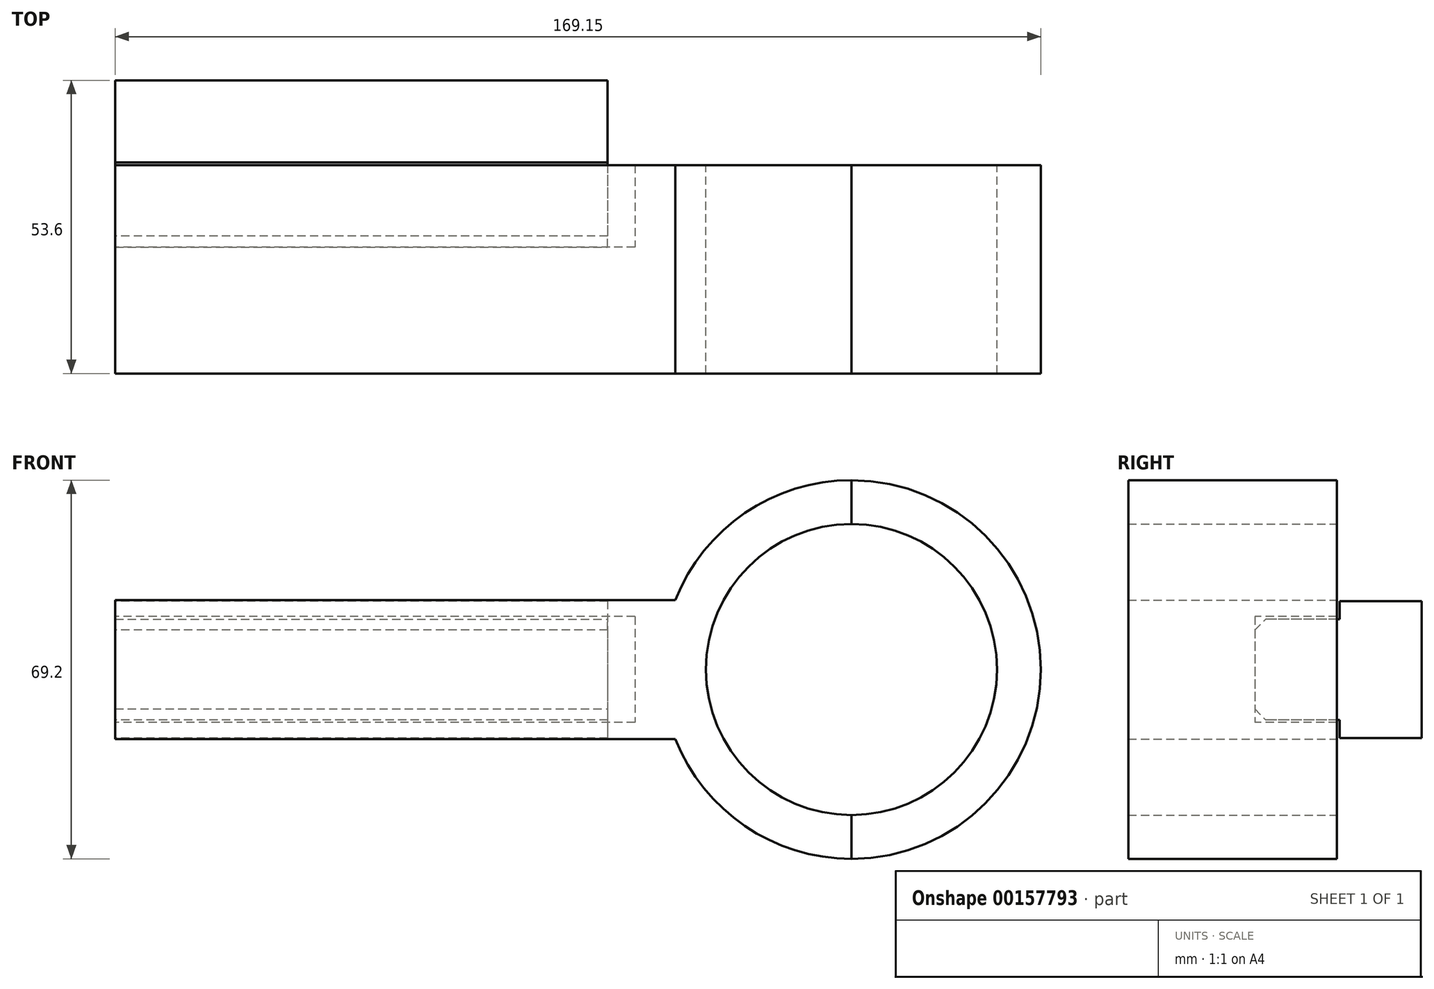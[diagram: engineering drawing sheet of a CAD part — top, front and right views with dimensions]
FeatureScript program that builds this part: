
annotation { "Feature Type Name" : "Feature", "Feature Type Description" : "" }
export const myFeature = defineFeature(function(context is Context, id is Id, definition is map)
    precondition{}
    {
        {
            var Q0;
            Q0=qCreatedBy(makeId("Front.planeOp"),FACE);
            var sketch = newSketch(context, id + "F0", { "sketchPlane" : qUnion([Q0])});
            skArc(sketch, "E0", {"start": v(0, 26.6) * mm, "mid": v(-26.6, 0) * mm, "end": v(0, -26.6) * mm});
            skLineSegment(sketch, "E1", {"start": v(0, 26.6) * mm, "end": v(0, 34.6) * mm});
            skLineSegment(sketch, "E2", {"start": v(0, -26.6) * mm, "end": v(0, -34.6) * mm});
            skArc(sketch, "E3", {"start": v(0, 34.6) * mm, "mid": v(-34.6, 0) * mm, "end": v(0, -34.6) * mm});
            skLineSegment(sketch, "E4.bottom", {"start": v(-134.55, 12.7) * mm, "end": v(-26.6, 12.7) * mm});
            skLineSegment(sketch, "E4.top", {"start": v(-134.55, -12.7) * mm, "end": v(-26.6, -12.7) * mm});
            skLineSegment(sketch, "E4.left", {"start": v(-134.55, 12.7) * mm, "end": v(-134.55, -12.7) * mm});
            skLineSegment(sketch, "E4.right", {"start": v(-26.6, 12.7) * mm, "end": v(-26.6, -12.7) * mm});
            skSolve(sketch);
        }
        {
            var Q0;
            {var subQ5=sQuery(id+"F0.wireOp",EDGE,"E4.left");Q0=makeQuery(id+"F0.imprint","IMPRINT",FACE,{"disambiguationData":[TD([[makeQuery(id+"F0.imprint","IMPRINT",EDGE,{"derivedFrom":subQ5}),1.0]])]});}
            var Q1;
            {var subQ1=sQuery(id+"F0.wireOp",EDGE,"E4.bottom");var subQ4=sQuery(id+"F0.wireOp",EDGE,"E3");var subQ5=makeQuery(id+"F0.imprint","INTERSECT",VERTEX,{"derivedFrom":[subQ4,subQ1]});Q1=makeQuery(id+"F0.imprint","IMPRINT",FACE,{"disambiguationData":[TD([[makeQuery(id+"F0.imprint","IMPRINT",EDGE,{"disambiguationData":[TD([[subQ5,-1.0]])],"derivedFrom":subQ4}),1.0]])]});}
            var Q2;
            {var subQ5=sQuery(id+"F0.wireOp",EDGE,"E1");Q2=makeQuery(id+"F0.imprint","IMPRINT",FACE,{"disambiguationData":[TD([[makeQuery(id+"F0.imprint","IMPRINT",EDGE,{"derivedFrom":subQ5}),1.0]])]});}
            var Q3;
            {var subQ5=sQuery(id+"F0.wireOp",EDGE,"E2");Q3=makeQuery(id+"F0.imprint","IMPRINT",FACE,{"disambiguationData":[TD([[makeQuery(id+"F0.imprint","IMPRINT",EDGE,{"derivedFrom":subQ5}),-1.0]])]});}
            extrude(context, id + "F1", {"entities" : qUnion([Q0, Q1, Q2, Q3]), "depth" : 38.1 * mm});
        }
        {
            var Q0;
            Q0=makeQuery(id+"F1.opExtrude","SWEPT_FACE",FACE,{"disambiguationData":[OSD([sQuery(id+"F0.wireOp",EDGE,"E4.left")])]});
            var sketch = newSketch(context, id + "F2", { "sketchPlane" : qUnion([Q0])});
            skLineSegment(sketch, "E5.bottom", {"start": v(0, 9.7) * mm, "end": v(15, 9.7) * mm});
            skLineSegment(sketch, "E5.top", {"start": v(0, -9.7) * mm, "end": v(15, -9.7) * mm});
            skLineSegment(sketch, "E5.left", {"start": v(0, 9.7) * mm, "end": v(0, -9.7) * mm});
            skLineSegment(sketch, "E5.right", {"start": v(15, 9.7) * mm, "end": v(15, -9.7) * mm});
            skSolve(sketch);
        }
        {
            var Q0;
            Q0=makeQuery(id+"F2.imprint","IMPRINT",FACE,{"disambiguationData":[TD([[makeQuery(id+"F2.imprint","IMPRINT",EDGE,{"derivedFrom":sQuery(id+"F2.wireOp",EDGE,"E5.bottom")}),-1.0]])]});
            extrude(context, id + "F3", {"entities" : qUnion([Q0]), "operationType" : NewBodyOperationType.REMOVE, "oppositeDirection" : true, "depth" : 95 * mm});
        }
        {
            var Q0;
            Q0=qCreatedBy(makeId("Front.planeOp"),FACE);
            var sketch = newSketch(context, id + "F4", { "sketchPlane" : qUnion([Q0])});
            skArc(sketch, "E6", {"start": v(0, -34.6) * mm, "mid": v(34.6, 0) * mm, "end": v(0, 34.6) * mm});
            skArc(sketch, "E7", {"start": v(0, -26.6) * mm, "mid": v(26.6, 0) * mm, "end": v(0, 26.6) * mm});
            skLineSegment(sketch, "E8", {"start": v(0, 34.6) * mm, "end": v(0, 26.6) * mm});
            skLineSegment(sketch, "E9", {"start": v(0, -26.6) * mm, "end": v(0, -34.6) * mm});
            skSolve(sketch);
        }
        {
            var Q0;
            Q0=makeQuery(id+"F4.imprint","IMPRINT",FACE,{"disambiguationData":[TD([[makeQuery(id+"F4.imprint","IMPRINT",EDGE,{"derivedFrom":sQuery(id+"F4.wireOp",EDGE,"E6")}),1.0]])]});
            var Q1;
            Q1=makeQuery(id+"F1.opExtrude","CAP_FACE",FACE,{"disambiguationData":[OSD([sQuery(id+"F0.wireOp",EDGE,"E0"),sQuery(id+"F0.wireOp",EDGE,"E1"),sQuery(id+"F0.wireOp",EDGE,"E2"),sQuery(id+"F0.wireOp",EDGE,"E3"),sQuery(id+"F0.wireOp",EDGE,"E4.bottom"),sQuery(id+"F0.wireOp",EDGE,"E4.top"),sQuery(id+"F0.wireOp",EDGE,"E4.left")])],"isStart":false});
            extrude(context, id + "F5", {"entities" : qUnion([Q0]), "endBound" : BoundingType.UP_TO_SURFACE, "endBoundEntityFace" : qUnion([Q1]), "depth" : 38.5 * mm});
        }
        {
            var Q0;
            Q0=makeQuery(id+"F1.opExtrude","SWEPT_FACE",FACE,{"disambiguationData":[OSD([sQuery(id+"F0.wireOp",EDGE,"E4.left")])]});
            var sketch = newSketch(context, id + "F6", { "sketchPlane" : qUnion([Q0])});
            skLineSegment(sketch, "E10.bottom", {"start": v(-15.5, 9.2) * mm, "end": v(15, 9.2) * mm});
            skLineSegment(sketch, "E10.top", {"start": v(-15.5, -9.2) * mm, "end": v(15, -9.2) * mm});
            skLineSegment(sketch, "E10.left", {"start": v(-15.5, 9.2) * mm, "end": v(-15.5, -9.2) * mm});
            skLineSegment(sketch, "E10.right", {"start": v(15, 9.2) * mm, "end": v(15, -9.2) * mm});
            skLineSegment(sketch, "E11.bottom", {"start": v(-15.5, 12.5) * mm, "end": v(-0.5, 12.5) * mm});
            skLineSegment(sketch, "E11.top", {"start": v(-15.5, -12.5) * mm, "end": v(-0.5, -12.5) * mm});
            skLineSegment(sketch, "E11.left", {"start": v(-15.5, 12.5) * mm, "end": v(-15.5, -12.5) * mm});
            skLineSegment(sketch, "E11.right", {"start": v(-0.5, 12.5) * mm, "end": v(-0.5, -12.5) * mm});
            skSolve(sketch);
        }
        {
            var Q0;
            {var subQ5=sQuery(id+"F6.wireOp",EDGE,"E11.top");Q0=makeQuery(id+"F6.imprint","IMPRINT",FACE,{"disambiguationData":[TD([[makeQuery(id+"F6.imprint","IMPRINT",EDGE,{"derivedFrom":subQ5}),1.0]])]});}
            var Q1;
            {var subQ0=sQuery(id+"F6.wireOp",EDGE,"E11.left");var subQ1=sQuery(id+"F6.wireOp",EDGE,"E10.bottom");var subQ2=makeQuery(id+"F6.imprint","INTERSECT",VERTEX,{"derivedFrom":[subQ1,subQ0]});Q1=makeQuery(id+"F6.imprint","IMPRINT",FACE,{"disambiguationData":[TD([[makeQuery(id+"F6.imprint","IMPRINT",EDGE,{"disambiguationData":[TD([[subQ2,-1.0]])],"derivedFrom":subQ1}),-1.0]])]});}
            var Q2;
            {var subQ5=sQuery(id+"F6.wireOp",EDGE,"E11.bottom");Q2=makeQuery(id+"F6.imprint","IMPRINT",FACE,{"disambiguationData":[TD([[makeQuery(id+"F6.imprint","IMPRINT",EDGE,{"derivedFrom":subQ5}),-1.0]])]});}
            var Q3;
            {var subQ0=sQuery(id+"F6.wireOp",EDGE,"E10.right");Q3=makeQuery(id+"F6.imprint","IMPRINT",FACE,{"disambiguationData":[TD([[makeQuery(id+"F6.imprint","IMPRINT",EDGE,{"derivedFrom":subQ0}),-1.0]])]});}
            extrude(context, id + "F7", {"entities" : qUnion([Q0, Q1, Q2, Q3]), "oppositeDirection" : true, "depth" : 90 * mm});
        }
        {
            var Q0;
            Q0=makeQuery(id+"F7.opExtrude","SWEPT_EDGE",EDGE,{"disambiguationData":[OSD([sQuery(id+"F2.wireOp",EDGE,"E5.right"),sQuery(id+"F6.wireOp",EDGE,"E10.top"),sQuery(id+"F6.wireOp",EDGE,"E10.right")])]});
            var Q1;
            Q1=makeQuery(id+"F7.opExtrude","SWEPT_EDGE",EDGE,{"disambiguationData":[OSD([sQuery(id+"F2.wireOp",EDGE,"E5.right"),sQuery(id+"F6.wireOp",EDGE,"E10.bottom"),sQuery(id+"F6.wireOp",EDGE,"E10.right")])]});
            chamfer(context, id + "F8", {"entities" : qUnion([Q0, Q1]), "width" : 2 * mm, "tangentPropagation" : true});
        }
    });
